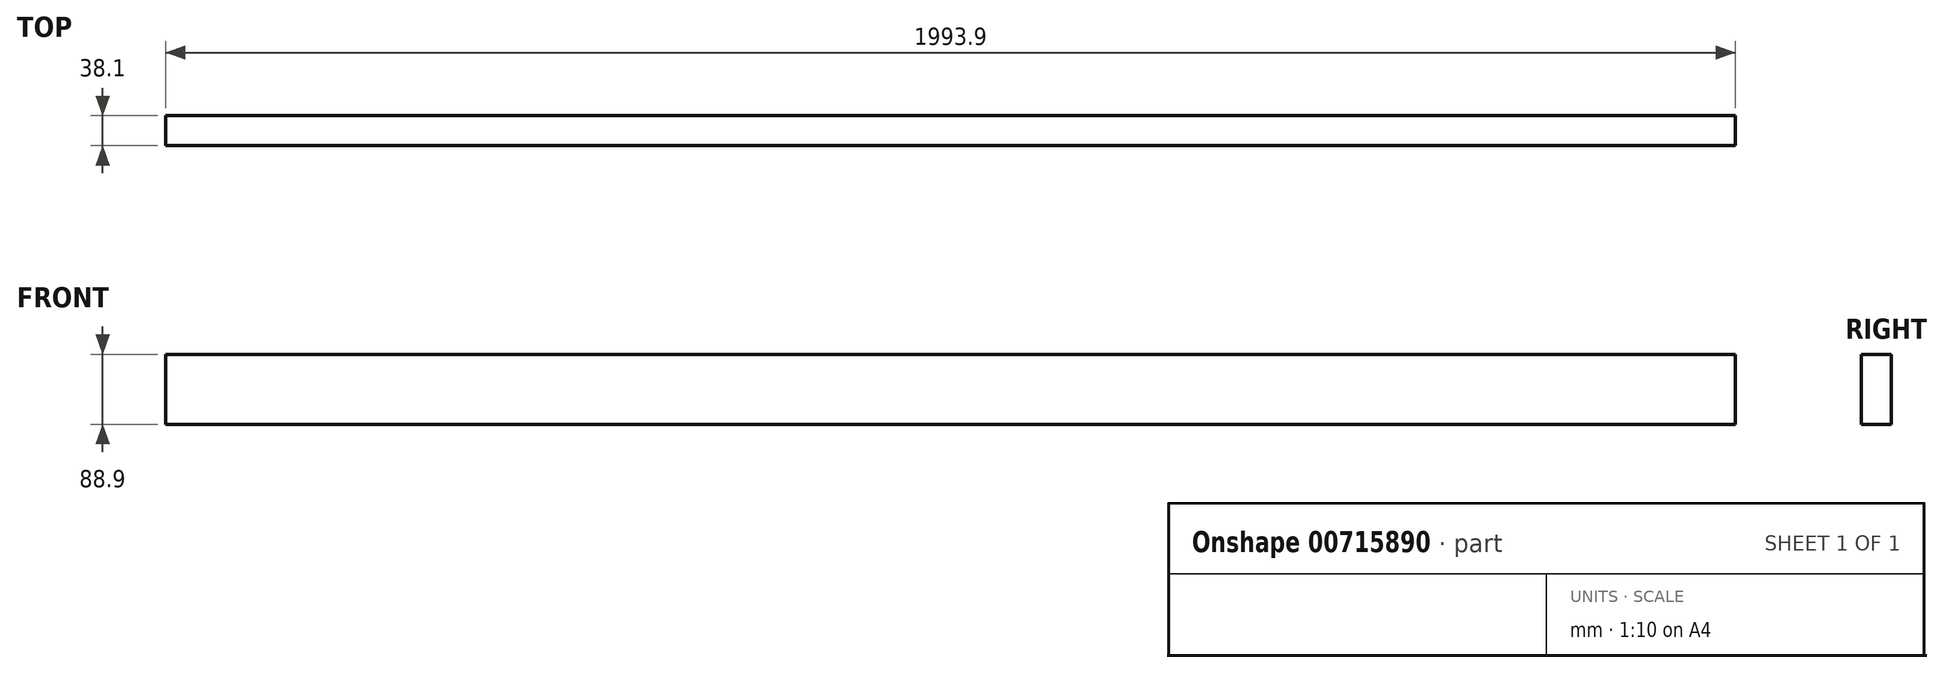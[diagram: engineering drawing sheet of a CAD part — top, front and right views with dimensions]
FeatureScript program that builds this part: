
annotation { "Feature Type Name" : "Feature", "Feature Type Description" : "" }
export const myFeature = defineFeature(function(context is Context, id is Id, definition is map)
    precondition{}
    {
        {
            var Q0;
            Q0=qCreatedBy(makeId("Right.planeOp"),FACE);
            var sketch = newSketch(context, id + "F0", { "sketchPlane" : qUnion([Q0])});
            skLineSegment(sketch, "E0.bottom", {"start": v(-19.05, 44.45) * mm, "end": v(19.05, 44.45) * mm});
            skLineSegment(sketch, "E0.top", {"start": v(-19.05, -44.45) * mm, "end": v(19.05, -44.45) * mm});
            skLineSegment(sketch, "E0.left", {"start": v(-19.05, 44.45) * mm, "end": v(-19.05, -44.45) * mm});
            skLineSegment(sketch, "E0.right", {"start": v(19.05, 44.45) * mm, "end": v(19.05, -44.45) * mm});
            skPoint(sketch, "E0.middle", {"position": v(0, 0) * mm});
            skSolve(sketch);
        }
        {
            var Q0;
            Q0 = qSketchRegion(id + "F0", true);
            extrude(context, id + "F1", {"entities" : qUnion([Q0]), "depth" : 1993.9 * mm, "offsetDistance" : 25.4 * mm, "symmetric" : true});
        }
    });
